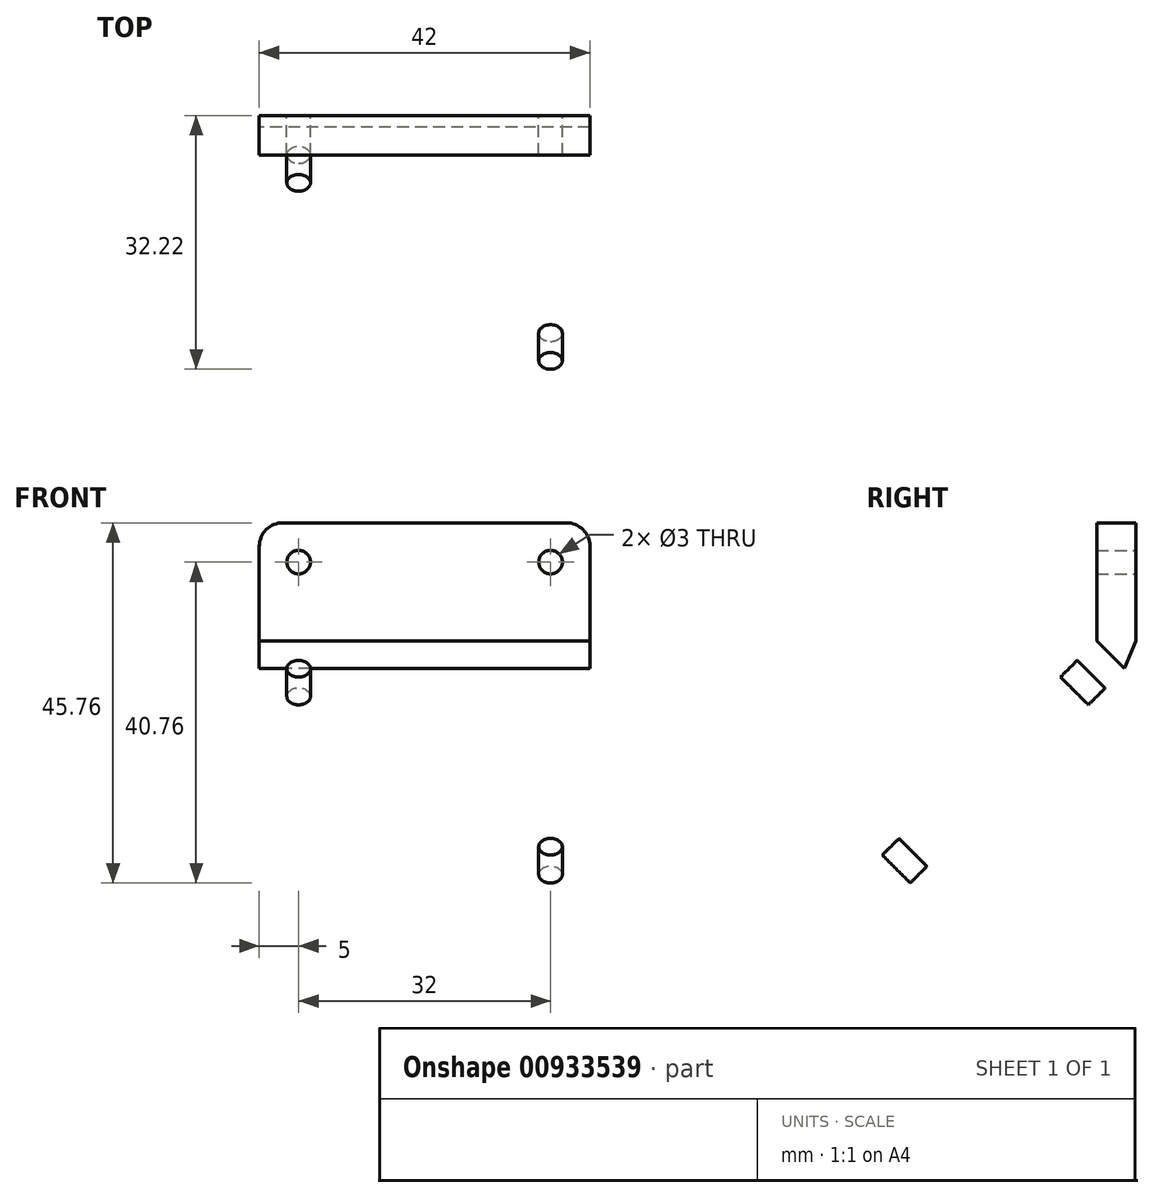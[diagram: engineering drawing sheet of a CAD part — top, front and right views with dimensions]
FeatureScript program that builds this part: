
annotation { "Feature Type Name" : "Feature", "Feature Type Description" : "" }
export const myFeature = defineFeature(function(context is Context, id is Id, definition is map)
    precondition{}
    {
        {
            var Q0;
            Q0=qCreatedBy(makeId("Front.planeOp"),FACE);
            var sketch = newSketch(context, id + "F0", { "sketchPlane" : qUnion([Q0])});
            skLineSegment(sketch, "E0.bottom", {"start": v(3, 0) * mm, "end": v(39, 0) * mm});
            skLineSegment(sketch, "E0.top", {"start": v(0, -15) * mm, "end": v(42, -15) * mm});
            skLineSegment(sketch, "E0.left", {"start": v(0, -3) * mm, "end": v(0, -15) * mm});
            skLineSegment(sketch, "E0.right", {"start": v(42, -3) * mm, "end": v(42, -15) * mm});
            skLineSegment(sketch, "E1", {"start": v(0, -7.5) * mm, "end": v(5, -7.5) * mm, "construction": true});
            skLineSegment(sketch, "E2", {"start": v(42, -7.5) * mm, "end": v(37, -7.5) * mm, "construction": true});
            skLineSegment(sketch, "E3", {"start": v(21, 0) * mm, "end": v(21, -5) * mm, "construction": true});
            skPoint(sketch, "E4.visualSharp", {"position": v(42, 0) * mm});
            skArc(sketch, "E4.filletArc", {"start": v(42, -3) * mm, "mid": v(41.12, -0.88) * mm, "end": v(39, 0) * mm});
            skPoint(sketch, "E5.visualSharp", {"position": v(0, 0) * mm});
            skArc(sketch, "E5.filletArc", {"start": v(3, 0) * mm, "mid": v(0.88, -0.88) * mm, "end": v(0, -3) * mm});
            skCircle(sketch, "E6", {"center": v(5, -5) * mm, "radius": 1.5 * mm});
            skCircle(sketch, "E7", {"center": v(37, -5) * mm, "radius": 1.5 * mm});
            skLineSegment(sketch, "E8", {"start": v(5, -5) * mm, "end": v(37, -5) * mm, "construction": true});
            skSolve(sketch);
        }
        {
            var Q0;
            Q0=makeQuery(id+"F0.imprint","IMPRINT",FACE,{"disambiguationData":[TD([[makeQuery(id+"F0.imprint","IMPRINT",EDGE,{"derivedFrom":sQuery(id+"F0.wireOp",EDGE,"E0.bottom")}),-1.0]])]});
            extrude(context, id + "F1", {"entities" : qUnion([Q0]), "depth" : 5 * mm, "offsetDistance" : 25 * mm});
        }
        {
            var Q0;
            Q0=makeQuery(id+"F1.opExtrude","SWEPT_FACE",FACE,{"disambiguationData":[OSD([sQuery(id+"F0.wireOp",EDGE,"E0.left")])]});
            var sketch = newSketch(context, id + "F2", { "sketchPlane" : qUnion([Q0])});
            skLineSegment(sketch, "E9", {"start": v(5, -15) * mm, "end": v(34.7, -44.7) * mm});
            skLineSegment(sketch, "E10", {"start": v(1.46, -18.54) * mm, "end": v(31.16, -48.23) * mm});
            skLineSegment(sketch, "E11", {"start": v(31.16, -48.23) * mm, "end": v(34.7, -44.7) * mm});
            skLineSegment(sketch, "E12", {"start": v(1.46, -18.54) * mm, "end": v(0, -15) * mm});
            skSolve(sketch);
        }
        {
            var Q0;
            Q0=makeQuery(id+"F2.imprint","IMPRINT",FACE,{"disambiguationData":[TD([[makeQuery(id+"F2.imprint","IMPRINT",EDGE,{"derivedFrom":sQuery(id+"F2.wireOp",EDGE,"E9")}),-1.0]])]});
            extrude(context, id + "F3", {"entities" : qUnion([Q0]), "operationType" : NewBodyOperationType.ADD, "oppositeDirection" : true, "depth" : 42 * mm, "offsetDistance" : 25 * mm});
        }
        {
            var Q0;
            Q0=makeQuery(id+"F3.opExtrude","SWEPT_FACE",FACE,{"disambiguationData":[OSD([sQuery(id+"F2.wireOp",EDGE,"E9")])]});
            var sketch = newSketch(context, id + "F4", { "sketchPlane" : qUnion([Q0])});
            skLineSegment(sketch, "E13", {"start": v(21, -14.14) * mm, "end": v(21, -56.14) * mm, "construction": true});
            skLineSegment(sketch, "E14", {"start": v(0, -35.14) * mm, "end": v(42, -35.14) * mm, "construction": true});
            skCircle(sketch, "E15", {"center": v(21, -35.14) * mm, "radius": 18 * mm});
            skLineSegment(sketch, "E16", {"start": v(21, -35.14) * mm, "end": v(21, -19.14) * mm, "construction": true});
            skLineSegment(sketch, "E17", {"start": v(21, -19.14) * mm, "end": v(37, -19.14) * mm, "construction": true});
            skCircle(sketch, "E18", {"center": v(37, -19.14) * mm, "radius": 1.5 * mm});
            skCircle(sketch, "E19.MirrorC", {"center": v(5, -19.14) * mm, "radius": 1.5 * mm});
            skCircle(sketch, "E20.MirrorC", {"center": v(37, -51.14) * mm, "radius": 1.5 * mm});
            skCircle(sketch, "E21.MirrorC", {"center": v(5, -51.14) * mm, "radius": 1.5 * mm});
            skSolve(sketch);
        }
        {
            var Q0;
            Q0=makeQuery(id+"F4.imprint","IMPRINT",FACE,{"disambiguationData":[TD([[makeQuery(id+"F4.imprint","IMPRINT",EDGE,{"derivedFrom":sQuery(id+"F4.wireOp",EDGE,"E18")}),1.0]])]});
            var Q1;
            Q1=makeQuery(id+"F4.imprint","IMPRINT",FACE,{"disambiguationData":[TD([[makeQuery(id+"F4.imprint","IMPRINT",EDGE,{"derivedFrom":sQuery(id+"F4.wireOp",EDGE,"E20.MirrorC")}),-1.0]])]});
            var Q2;
            Q2=makeQuery(id+"F4.imprint","IMPRINT",FACE,{"disambiguationData":[TD([[makeQuery(id+"F4.imprint","IMPRINT",EDGE,{"derivedFrom":sQuery(id+"F4.wireOp",EDGE,"E21.MirrorC")}),1.0]])]});
            var Q3;
            Q3=makeQuery(id+"F4.imprint","IMPRINT",FACE,{"disambiguationData":[TD([[makeQuery(id+"F4.imprint","IMPRINT",EDGE,{"derivedFrom":sQuery(id+"F4.wireOp",EDGE,"E19.MirrorC")}),-1.0]])]});
            var Q4;
            Q4=makeQuery(id+"F4.imprint","IMPRINT",FACE,{"disambiguationData":[TD([[makeQuery(id+"F4.imprint","IMPRINT",EDGE,{"derivedFrom":sQuery(id+"F4.wireOp",EDGE,"E15")}),1.0]])]});
            extrude(context, id + "F5", {"entities" : qUnion([Q0, Q1, Q2, Q3, Q4]), "operationType" : NewBodyOperationType.REMOVE, "oppositeDirection" : true, "depth" : 5 * mm, "offsetDistance" : 25 * mm});
        }
    });
